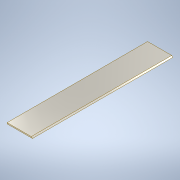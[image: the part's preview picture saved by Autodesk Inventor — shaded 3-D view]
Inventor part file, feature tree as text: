
AUTODESK INVENTOR PART (.ipt)
format: ipt  version: 2020 (Build 240168000, 168)  size: 101,888 bytes
history: native  units: in
note: dims shown in document units (in); Inventor stores cm internally (conversion verified against a paired STEP export)
features: extrude x1, chamfer x1, sketch x1
ambient origin geometry x8: Origin, YZ Plane, XZ Plane, XY Plane, X Axis, Y Axis, Z Axis, Center Point
bodies: Solid1 (feature_tree)
feature tree (3):
  extrude  "Extrusion1"  Depth=0.0315in
  chamfer  "Chamfer1"  Distance=3.937in
  sketch  "Sketch1"  dims[d0=0.7087in d1=0.3543in d2=3.937in d3=1.9685in d4=0.0315in d5=0.0in d6=0.0315in d7=0.0492in d8=45.0deg]
